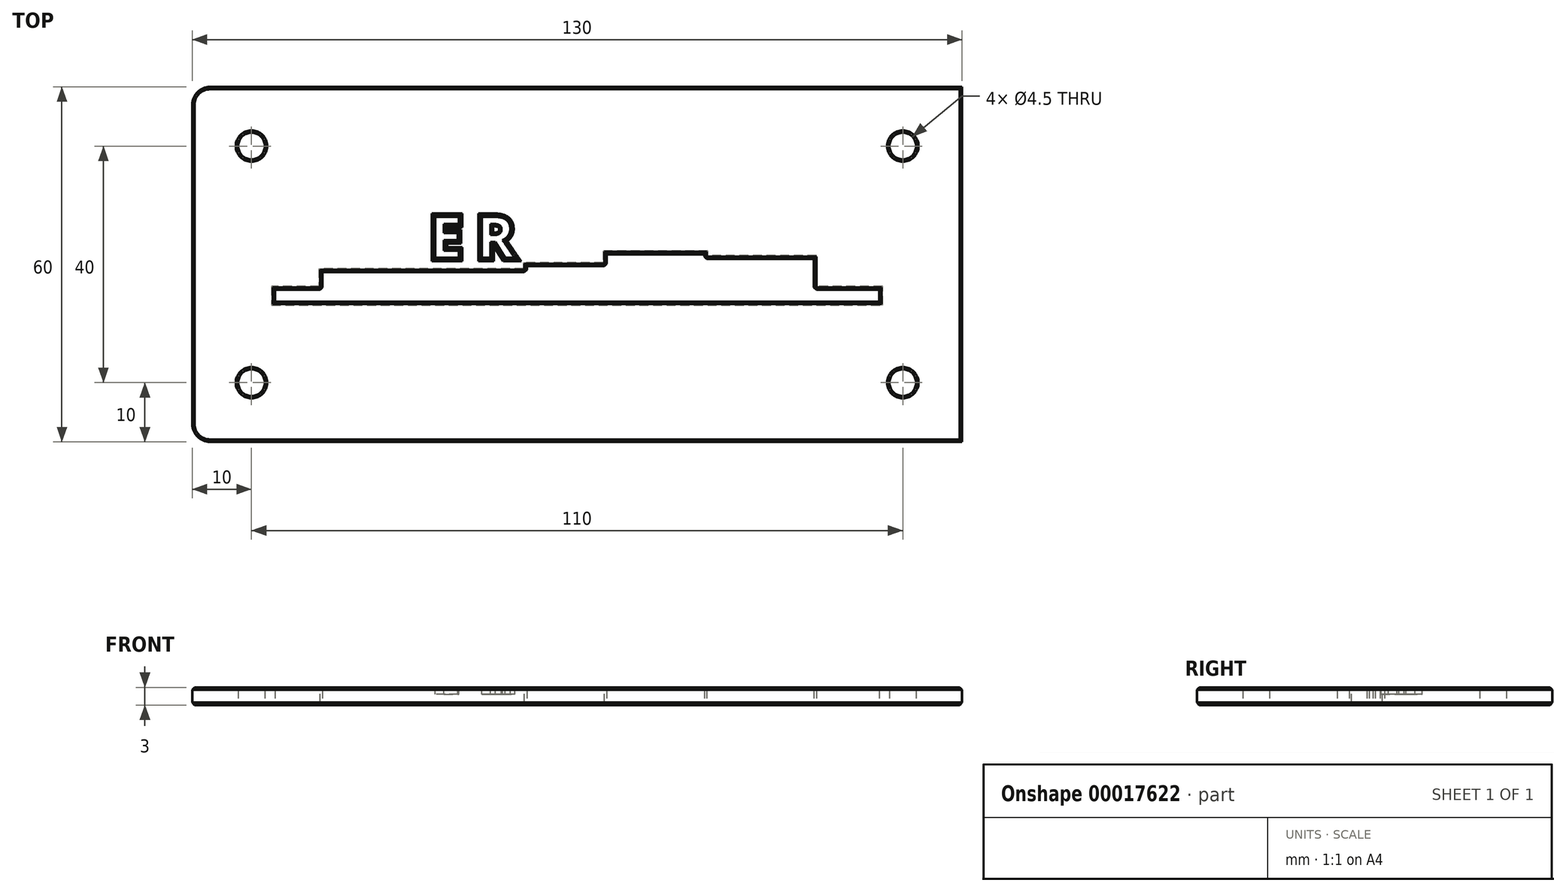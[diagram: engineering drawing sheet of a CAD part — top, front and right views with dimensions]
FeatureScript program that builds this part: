
annotation { "Feature Type Name" : "Feature", "Feature Type Description" : "" }
export const myFeature = defineFeature(function(context is Context, id is Id, definition is map)
    precondition{}
    {
        {
            var Q0;
            Q0=qCreatedBy(makeId("Top.planeOp"),FACE);
            var sketch = newSketch(context, id + "F0", { "sketchPlane" : qUnion([Q0])});
            skLineSegment(sketch, "E0.rect.top", {"start": v(-60, 30) * mm, "end": v(65, 30) * mm});
            skLineSegment(sketch, "E0.rect.right", {"start": v(65, -30) * mm, "end": v(65, 30) * mm});
            skPoint(sketch, "E0.rect.middle", {"position": v(0, 0) * mm});
            skLineSegment(sketch, "E1.bottom", {"start": v(-65, 30) * mm, "end": v(-60, 30) * mm});
            skLineSegment(sketch, "E2.bottom", {"start": v(65, 30) * mm, "end": v(55, 30) * mm});
            skLineSegment(sketch, "E2.left", {"start": v(65, 30) * mm, "end": v(65, 22.5) * mm});
            skLineSegment(sketch, "E3.left", {"start": v(65, -30) * mm, "end": v(65, -22.5) * mm});
            skCircle(sketch, "E4", {"center": v(-55, -20) * mm, "radius": 2.25 * mm});
            skCircle(sketch, "E5", {"center": v(-55, 20) * mm, "radius": 2.25 * mm});
            skCircle(sketch, "E6", {"center": v(55, 20) * mm, "radius": 2.25 * mm});
            skCircle(sketch, "E7", {"center": v(55, -20) * mm, "radius": 2.25 * mm});
            skLineSegment(sketch, "E8", {"start": v(-51, 6.3) * mm, "end": v(1.5, 6.3) * mm});
            skLineSegment(sketch, "E9.top", {"start": v(-51, 4.3) * mm, "end": v(-43, 4.3) * mm});
            skLineSegment(sketch, "E9.left", {"start": v(-51, 6.3) * mm, "end": v(-51, 4.3) * mm});
            skLineSegment(sketch, "E9.right", {"start": v(51, 6.3) * mm, "end": v(51, 4.3) * mm});
            skLineSegment(sketch, "E10.top", {"start": v(-43, 1.3) * mm, "end": v(-8.5, 1.3) * mm});
            skLineSegment(sketch, "E10.left", {"start": v(-43, 4.3) * mm, "end": v(-43, 1.3) * mm});
            skLineSegment(sketch, "E11.trimOffspring", {"start": v(43, 4.3) * mm, "end": v(51, 4.3) * mm});
            skLineSegment(sketch, "E12.right", {"start": v(-8.5, 1.3) * mm, "end": v(-8.5, 0.3) * mm});
            skLineSegment(sketch, "E13.left", {"start": v(-8.5, 0.3) * mm, "end": v(-8.5, 1.3) * mm});
            skLineSegment(sketch, "E14.top", {"start": v(-8.5, 0.3) * mm, "end": v(1.5, 0.3) * mm});
            skLineSegment(sketch, "E15.right", {"start": v(21.5, 1.3) * mm, "end": v(21.5, 1.6) * mm});
            skLineSegment(sketch, "E16.top", {"start": v(5, -1.7) * mm, "end": v(21.5, -1.7) * mm});
            skLineSegment(sketch, "E16.right", {"start": v(21.5, -0.9) * mm, "end": v(21.5, -1.7) * mm});
            skLineSegment(sketch, "E17.trimOffspring", {"start": v(5, 6.3) * mm, "end": v(21.5, 6.3) * mm});
            skLineSegment(sketch, "E18.trimOffspring", {"start": v(25, 6.3) * mm, "end": v(51, 6.3) * mm});
            skLineSegment(sketch, "E19", {"start": v(-43, 4.3) * mm, "end": v(5, 4.3) * mm, "construction": true});
            skLineSegment(sketch, "E20", {"start": v(1.5, 6.3) * mm, "end": v(5, 6.3) * mm});
            skLineSegment(sketch, "E21", {"start": v(21.5, 6.3) * mm, "end": v(25, 6.3) * mm});
            skLineSegment(sketch, "E22.bottom", {"start": v(43, 4.3) * mm, "end": v(40, 4.3) * mm});
            skLineSegment(sketch, "E22.right", {"start": v(40, 4.3) * mm, "end": v(40, 1.6) * mm});
            skPoint(sketch, "E23.oppositeSnap0", {"position": v(25, 1.6) * mm});
            skPoint(sketch, "E24.orphan", {"position": v(43, -10) * mm});
            skLineSegment(sketch, "E25.trimOffspring", {"start": v(40, 4.3) * mm, "end": v(43, 4.3) * mm, "construction": true});
            skPoint(sketch, "E26.orphan", {"position": v(25, -10.7) * mm});
            skPoint(sketch, "E27.right.start.orphan", {"position": v(25, 13.9) * mm});
            skPoint(sketch, "E28.end.orphan", {"position": v(23, 3.6) * mm});
            skLineSegment(sketch, "E29.top", {"start": v(4.98, 0.3) * mm, "end": v(1.5, 0.3) * mm});
            skLineSegment(sketch, "E30", {"start": v(4.98, 0.3) * mm, "end": v(5, -1.7) * mm});
            skLineSegment(sketch, "E31.top", {"start": v(21.5, -0.9) * mm, "end": v(40, -0.9) * mm});
            skLineSegment(sketch, "E31.right", {"start": v(40, 1.6) * mm, "end": v(40, -0.9) * mm});
            skPoint(sketch, "E32.start.orphan", {"position": v(23, 1.6) * mm});
            skLineSegment(sketch, "E33", {"start": v(-65, 30) * mm, "end": v(-65, -30) * mm});
            skPoint(sketch, "E34.orphan", {"position": v(-65, -30) * mm});
            skPoint(sketch, "E0.rect.bottom.start.orphan", {"position": v(60, -30) * mm});
            skLineSegment(sketch, "E35", {"start": v(-65, -30) * mm, "end": v(65, -30) * mm});
            skSolve(sketch);
        }
        {
            var Q0;
            Q0=makeQuery(id+"F0.imprint","IMPRINT",FACE,{"disambiguationData":[TD([[makeQuery(id+"F0.imprint","IMPRINT",EDGE,{"derivedFrom":sQuery(id+"F0.wireOp",EDGE,"E0.rect.bottom")}),1.0]])]});
            var Q1;
            Q1=makeQuery(id+"F0.imprint","IMPRINT",FACE,{"disambiguationData":[TD([[makeQuery(id+"F0.imprint","IMPRINT",EDGE,{"derivedFrom":sQuery(id+"F0.wireOp",EDGE,"E0.rect.top")}),-1.0]])]});
            extrude(context, id + "F1", {"entities" : qUnion([Q0, Q1]), "oppositeDirection" : true, "depth" : 3 * mm, "offsetDistance" : 25 * mm});
        }
        {
            var Q0;
            Q0=makeQuery(id+"F1.opExtrude","SWEPT_EDGE",EDGE,{"disambiguationData":[OSD([sQuery(id+"F0.wireOp",EDGE,"E3.bottom"),sQuery(id+"F0.wireOp",EDGE,"E3.left")])]});
            var Q1;
            Q1=makeQuery(id+"F1.opExtrude","SWEPT_EDGE",EDGE,{"disambiguationData":[OSD([sQuery(id+"F0.wireOp",EDGE,"fb71736d-f74a-4242-934e-06f3cf912558.bottom"),sQuery(id+"F0.wireOp",EDGE,"fb71736d-f74a-4242-934e-06f3cf912558.left")])]});
            var Q2;
            Q2=makeQuery(id+"F1.opExtrude","SWEPT_EDGE",EDGE,{"disambiguationData":[OSD([sQuery(id+"F0.wireOp",EDGE,"E2.bottom"),sQuery(id+"F0.wireOp",EDGE,"E2.left")])]});
            var Q3;
            Q3=makeQuery(id+"F1.opExtrude","SWEPT_EDGE",EDGE,{"disambiguationData":[OSD([sQuery(id+"F0.wireOp",EDGE,"E1.bottom"),sQuery(id+"F0.wireOp",EDGE,"E1.left")])]});
            var Q4;
            Q4=makeQuery(id+"F1.opExtrude","SWEPT_EDGE",EDGE,{"disambiguationData":[OSD([sQuery(id+"F0.wireOp",EDGE,"E33"),sQuery(id+"F0.wireOp",EDGE,"E35")])]});
            fillet(context, id + "F2", {"entities" : qUnion([Q0, Q1, Q2, Q3, Q4]), "radius" : 3 * mm, "tangentPropagation" : true, "allowEdgeOverflow" : false});
        }
        {
            var Q0;
            Q0=makeQuery(id+"F1.opExtrude","CAP_FACE",FACE,{"disambiguationData":[OSD([sQuery(id+"F0.wireOp",EDGE,"E0.rect.bottom"),sQuery(id+"F0.wireOp",EDGE,"E0.rect.top"),sQuery(id+"F0.wireOp",EDGE,"E0.rect.left"),sQuery(id+"F0.wireOp",EDGE,"E0.rect.right"),sQuery(id+"F0.wireOp",EDGE,"fb71736d-f74a-4242-934e-06f3cf912558.bottom"),sQuery(id+"F0.wireOp",EDGE,"fb71736d-f74a-4242-934e-06f3cf912558.left"),sQuery(id+"F0.wireOp",EDGE,"E1.bottom"),sQuery(id+"F0.wireOp",EDGE,"E1.left"),sQuery(id+"F0.wireOp",EDGE,"E2.bottom"),sQuery(id+"F0.wireOp",EDGE,"E2.left"),sQuery(id+"F0.wireOp",EDGE,"E3.bottom"),sQuery(id+"F0.wireOp",EDGE,"E3.left"),sQuery(id+"F0.wireOp",EDGE,"E4"),sQuery(id+"F0.wireOp",EDGE,"E5"),sQuery(id+"F0.wireOp",EDGE,"E6"),sQuery(id+"F0.wireOp",EDGE,"E7"),sQuery(id+"F0.wireOp",EDGE,"E8"),sQuery(id+"F0.wireOp",EDGE,"E9.top"),sQuery(id+"F0.wireOp",EDGE,"E9.left"),sQuery(id+"F0.wireOp",EDGE,"E9.right"),sQuery(id+"F0.wireOp",EDGE,"E10.left"),sQuery(id+"F0.wireOp",EDGE,"E10.right"),sQuery(id+"F0.wireOp",EDGE,"E11.trimOffspring"),sQuery(id+"F0.wireOp",EDGE,"E10.top"),sQuery(id+"F0.wireOp",EDGE,"E13.bottom"),sQuery(id+"F0.wireOp",EDGE,"E13.left"),sQuery(id+"F0.wireOp",EDGE,"E13.right"),sQuery(id+"F0.wireOp",EDGE,"2bbd994b-3e8e-4b0d-a158-f2154df3f7ed.trimOffspring"),sQuery(id+"F0.wireOp",EDGE,"E27.top"),sQuery(id+"F0.wireOp",EDGE,"E27.left"),sQuery(id+"F0.wireOp",EDGE,"E27.right")])],"isStart":false});
            var sketch = newSketch(context, id + "F3", { "sketchPlane" : qUnion([Q0])});
            skText(sketch, "E36", { "text": "E", "fontName": "OpenSans-Bold.ttf"});
            skText(sketch, "E37", { "text": "R", "fontName": "OpenSans-Bold.ttf"});
            skPoint(sketch, "E38.right.start.orphan", {"position": v(-26.9, 1.1) * mm});
            skPoint(sketch, "E39.orphan", {"position": v(-8.9, -0.9) * mm});
            skPoint(sketch, "E38.bottom.end.orphan", {"position": v(-26.9, -0.9) * mm});
            skPoint(sketch, "E38.bottom.start.orphan", {"position": v(-17.9, -0.9) * mm});
            skLineSegment(sketch, "E40", {"start": v(-43, -1.3) * mm, "end": v(-8.5, -1.3) * mm});
            const initialGuessF3  = {"E36": [-0.02483, 0.0011, 1, 0, 0.007], "E37": [-0.01696, 0.0011, 1, 0, 0.007]};
            skSetInitialGuess(sketch, initialGuessF3);
            skSolve(sketch);
        }
        {
            var Q0;
            Q0=makeQuery(id+"F3.imprint","IMPRINT",FACE,{"disambiguationData":[TD([[makeQuery(id+"F3.imprint","IMPRINT",EDGE,{"derivedFrom":sQuery(id+"F3.wireOp",EDGE,"E36.sketch_text.stroke-0")}),-1.0]])]});
            var Q1;
            Q1=makeQuery(id+"F3.imprint","IMPRINT",FACE,{"disambiguationData":[TD([[makeQuery(id+"F3.imprint","IMPRINT",EDGE,{"derivedFrom":sQuery(id+"F3.wireOp",EDGE,"E37.sketch_text.stroke-0")}),-1.0]])]});
            extrude(context, id + "F4", {"entities" : qUnion([Q0, Q1]), "operationType" : NewBodyOperationType.REMOVE, "oppositeDirection" : true, "depth" : 1.2 * mm});
        }
        {
            var Q0;
            Q0=makeQuery(id+"F4.boolean.opBoolean","COPY",EDGE,{"derivedFrom":makeQuery(id+"F4.opExtrude","CAP_EDGE",EDGE,{"disambiguationData":[OSD([sQuery(id+"F3.wireOp",EDGE,"E36.sketch_text.stroke-1")])],"isStart":true})});
            var Q1;
            Q1=makeQuery(id+"F4.boolean.opBoolean","COPY",EDGE,{"derivedFrom":makeQuery(id+"F4.opExtrude","CAP_EDGE",EDGE,{"disambiguationData":[OSD([sQuery(id+"F3.wireOp",EDGE,"E36.sketch_text.stroke-2")])],"isStart":true})});
            var Q2;
            Q2=makeQuery(id+"F4.boolean.opBoolean","COPY",EDGE,{"derivedFrom":makeQuery(id+"F4.opExtrude","CAP_EDGE",EDGE,{"disambiguationData":[OSD([sQuery(id+"F3.wireOp",EDGE,"E36.sketch_text.stroke-3")])],"isStart":true})});
            var Q3;
            Q3=makeQuery(id+"F4.boolean.opBoolean","COPY",EDGE,{"derivedFrom":makeQuery(id+"F4.opExtrude","CAP_EDGE",EDGE,{"disambiguationData":[OSD([sQuery(id+"F3.wireOp",EDGE,"E36.sketch_text.stroke-4")])],"isStart":true})});
            var Q4;
            Q4=makeQuery(id+"F4.boolean.opBoolean","COPY",EDGE,{"derivedFrom":makeQuery(id+"F4.opExtrude","CAP_EDGE",EDGE,{"disambiguationData":[OSD([sQuery(id+"F3.wireOp",EDGE,"E36.sketch_text.stroke-5")])],"isStart":true})});
            var Q5;
            Q5=makeQuery(id+"F4.boolean.opBoolean","COPY",EDGE,{"derivedFrom":makeQuery(id+"F4.opExtrude","CAP_EDGE",EDGE,{"disambiguationData":[OSD([sQuery(id+"F3.wireOp",EDGE,"E36.sketch_text.stroke-6")])],"isStart":true})});
            var Q6;
            Q6=makeQuery(id+"F4.boolean.opBoolean","COPY",EDGE,{"derivedFrom":makeQuery(id+"F4.opExtrude","CAP_EDGE",EDGE,{"disambiguationData":[OSD([sQuery(id+"F3.wireOp",EDGE,"E36.sketch_text.stroke-7")])],"isStart":true})});
            var Q7;
            Q7=makeQuery(id+"F4.boolean.opBoolean","COPY",EDGE,{"derivedFrom":makeQuery(id+"F4.opExtrude","CAP_EDGE",EDGE,{"disambiguationData":[OSD([sQuery(id+"F3.wireOp",EDGE,"E36.sketch_text.stroke-8")])],"isStart":true})});
            var Q8;
            Q8=makeQuery(id+"F4.boolean.opBoolean","COPY",EDGE,{"derivedFrom":makeQuery(id+"F4.opExtrude","CAP_EDGE",EDGE,{"disambiguationData":[OSD([sQuery(id+"F3.wireOp",EDGE,"E36.sketch_text.stroke-9")])],"isStart":true})});
            var Q9;
            Q9=makeQuery(id+"F4.boolean.opBoolean","COPY",EDGE,{"derivedFrom":makeQuery(id+"F4.opExtrude","CAP_EDGE",EDGE,{"disambiguationData":[OSD([sQuery(id+"F3.wireOp",EDGE,"E36.sketch_text.stroke-10")])],"isStart":true})});
            var Q10;
            Q10=makeQuery(id+"F4.boolean.opBoolean","COPY",EDGE,{"derivedFrom":makeQuery(id+"F4.opExtrude","CAP_EDGE",EDGE,{"disambiguationData":[OSD([sQuery(id+"F3.wireOp",EDGE,"E36.sketch_text.stroke-11")])],"isStart":true})});
            var Q11;
            Q11=makeQuery(id+"F4.boolean.opBoolean","COPY",EDGE,{"derivedFrom":makeQuery(id+"F4.opExtrude","CAP_EDGE",EDGE,{"disambiguationData":[OSD([sQuery(id+"F3.wireOp",EDGE,"E36.sketch_text.stroke-0")])],"isStart":true})});
            var Q12;
            Q12=makeQuery(id+"F4.boolean.opBoolean","COPY",EDGE,{"derivedFrom":makeQuery(id+"F4.opExtrude","CAP_EDGE",EDGE,{"disambiguationData":[OSD([sQuery(id+"F3.wireOp",EDGE,"E37.sketch_text.stroke-9")])],"isStart":true})});
            var Q13;
            Q13=makeQuery(id+"F4.boolean.opBoolean","COPY",EDGE,{"derivedFrom":makeQuery(id+"F4.opExtrude","CAP_EDGE",EDGE,{"disambiguationData":[OSD([sQuery(id+"F3.wireOp",EDGE,"E37.sketch_text.stroke-8")])],"isStart":true})});
            var Q14;
            Q14=makeQuery(id+"F4.boolean.opBoolean","COPY",EDGE,{"derivedFrom":makeQuery(id+"F4.opExtrude","CAP_EDGE",EDGE,{"disambiguationData":[OSD([sQuery(id+"F3.wireOp",EDGE,"E37.sketch_text.stroke-7")])],"isStart":true})});
            var Q15;
            Q15=makeQuery(id+"F4.boolean.opBoolean","COPY",EDGE,{"derivedFrom":makeQuery(id+"F4.opExtrude","CAP_EDGE",EDGE,{"disambiguationData":[OSD([sQuery(id+"F3.wireOp",EDGE,"E37.sketch_text.stroke-18")])],"isStart":true})});
            var Q16;
            Q16=makeQuery(id+"F4.boolean.opBoolean","COPY",EDGE,{"derivedFrom":makeQuery(id+"F4.opExtrude","CAP_EDGE",EDGE,{"disambiguationData":[OSD([sQuery(id+"F3.wireOp",EDGE,"E37.sketch_text.stroke-17")])],"isStart":true})});
            var Q17;
            Q17=makeQuery(id+"F4.boolean.opBoolean","COPY",EDGE,{"derivedFrom":makeQuery(id+"F4.opExtrude","CAP_EDGE",EDGE,{"disambiguationData":[OSD([sQuery(id+"F3.wireOp",EDGE,"E37.sketch_text.stroke-16")])],"isStart":true})});
            var Q18;
            Q18=makeQuery(id+"F4.boolean.opBoolean","COPY",EDGE,{"derivedFrom":makeQuery(id+"F4.opExtrude","CAP_EDGE",EDGE,{"disambiguationData":[OSD([sQuery(id+"F3.wireOp",EDGE,"E37.sketch_text.stroke-15")])],"isStart":true})});
            var Q19;
            Q19=makeQuery(id+"F4.boolean.opBoolean","COPY",EDGE,{"derivedFrom":makeQuery(id+"F4.opExtrude","CAP_EDGE",EDGE,{"disambiguationData":[OSD([sQuery(id+"F3.wireOp",EDGE,"E37.sketch_text.stroke-14")])],"isStart":true})});
            var Q20;
            Q20=makeQuery(id+"F4.boolean.opBoolean","COPY",EDGE,{"derivedFrom":makeQuery(id+"F4.opExtrude","CAP_EDGE",EDGE,{"disambiguationData":[OSD([sQuery(id+"F3.wireOp",EDGE,"E37.sketch_text.stroke-13")])],"isStart":true})});
            var Q21;
            Q21=makeQuery(id+"F4.boolean.opBoolean","COPY",EDGE,{"derivedFrom":makeQuery(id+"F4.opExtrude","CAP_EDGE",EDGE,{"disambiguationData":[OSD([sQuery(id+"F3.wireOp",EDGE,"E37.sketch_text.stroke-12")])],"isStart":true})});
            var Q22;
            Q22=makeQuery(id+"F4.boolean.opBoolean","COPY",EDGE,{"derivedFrom":makeQuery(id+"F4.opExtrude","CAP_EDGE",EDGE,{"disambiguationData":[OSD([sQuery(id+"F3.wireOp",EDGE,"E37.sketch_text.stroke-11")])],"isStart":true})});
            var Q23;
            Q23=makeQuery(id+"F4.boolean.opBoolean","COPY",EDGE,{"derivedFrom":makeQuery(id+"F4.opExtrude","CAP_EDGE",EDGE,{"disambiguationData":[OSD([sQuery(id+"F3.wireOp",EDGE,"E37.sketch_text.stroke-10")])],"isStart":true})});
            var Q24;
            Q24=makeQuery(id+"F4.boolean.opBoolean","SPLIT",FACE,{"disambiguationData":[TD([makeQuery(id+"F4.opExtrude","SWEPT_FACE",FACE,{"disambiguationData":[OSD([sQuery(id+"F3.wireOp",EDGE,"E37.sketch_text.stroke-0")])]})])],"derivedFrom":makeQuery(id+"F1.opExtrude","CAP_FACE",FACE,{"disambiguationData":[OSD([sQuery(id+"F0.wireOp",EDGE,"E0.rect.bottom"),sQuery(id+"F0.wireOp",EDGE,"E0.rect.top"),sQuery(id+"F0.wireOp",EDGE,"E0.rect.left"),sQuery(id+"F0.wireOp",EDGE,"E0.rect.right"),sQuery(id+"F0.wireOp",EDGE,"fb71736d-f74a-4242-934e-06f3cf912558.left"),sQuery(id+"F0.wireOp",EDGE,"E1.bottom"),sQuery(id+"F0.wireOp",EDGE,"E1.left"),sQuery(id+"F0.wireOp",EDGE,"E2.bottom"),sQuery(id+"F0.wireOp",EDGE,"E2.left"),sQuery(id+"F0.wireOp",EDGE,"E3.bottom"),sQuery(id+"F0.wireOp",EDGE,"E3.left"),sQuery(id+"F0.wireOp",EDGE,"E4"),sQuery(id+"F0.wireOp",EDGE,"E5"),sQuery(id+"F0.wireOp",EDGE,"E6"),sQuery(id+"F0.wireOp",EDGE,"E7"),sQuery(id+"F0.wireOp",EDGE,"E8"),sQuery(id+"F0.wireOp",EDGE,"E9.top"),sQuery(id+"F0.wireOp",EDGE,"E9.left"),sQuery(id+"F0.wireOp",EDGE,"E9.right"),sQuery(id+"F0.wireOp",EDGE,"E10.left"),sQuery(id+"F0.wireOp",EDGE,"E10.right"),sQuery(id+"F0.wireOp",EDGE,"E11.trimOffspring"),sQuery(id+"F0.wireOp",EDGE,"E10.top"),sQuery(id+"F0.wireOp",EDGE,"E27.top"),sQuery(id+"F0.wireOp",EDGE,"E27.left"),sQuery(id+"F0.wireOp",EDGE,"E27.right"),sQuery(id+"F0.wireOp",EDGE,"E14.top"),sQuery(id+"F0.wireOp",EDGE,"E12.right"),sQuery(id+"F0.wireOp",EDGE,"E14.right"),sQuery(id+"F0.wireOp",EDGE,"c10e0dd7-fc39-4358-877f-853744283f95"),sQuery(id+"F0.wireOp",EDGE,"E15.left"),sQuery(id+"F0.wireOp",EDGE,"E15.right"),sQuery(id+"F0.wireOp",EDGE,"b61ca566-ba07-4bff-9836-ffdb72489c4c.left"),sQuery(id+"F0.wireOp",EDGE,"b61ca566-ba07-4bff-9836-ffdb72489c4c.right"),sQuery(id+"F0.wireOp",EDGE,"E16.top"),sQuery(id+"F0.wireOp",EDGE,"E16.left"),sQuery(id+"F0.wireOp",EDGE,"E16.right"),sQuery(id+"F0.wireOp",EDGE,"E17.trimOffspring"),sQuery(id+"F0.wireOp",EDGE,"E18.trimOffspring"),sQuery(id+"F0.wireOp",EDGE,"54661143-fa5e-42c1-9d10-70f3552f3fbd"),sQuery(id+"F0.wireOp",EDGE,"E28"),sQuery(id+"F0.wireOp",EDGE,"E20"),sQuery(id+"F0.wireOp",EDGE,"E21")])],"isStart":false})});
            chamfer(context, id + "F5", {"entities" : qUnion([Q0, Q1, Q2, Q3, Q4, Q5, Q6, Q7, Q8, Q9, Q10, Q11, Q12, Q13, Q14, Q15, Q16, Q17, Q18, Q19, Q20, Q21, Q22, Q23, Q24]), "width" : .4 * mm});
        }
        {
            var Q0;
            Q0=makeQuery(id+"F1.opExtrude","CAP_EDGE",EDGE,{"disambiguationData":[OSD([sQuery(id+"F0.wireOp",EDGE,"E0.rect.bottom"),sQuery(id+"F0.wireOp",EDGE,"E3.bottom"),sQuery(id+"F0.wireOp",EDGE,"c10e0dd7-fc39-4358-877f-853744283f95")])],"isStart":false});
            var Q1;
            {var subQ0=sQuery(id+"F0.wireOp",EDGE,"fb71736d-f74a-4242-934e-06f3cf912558.left");var subQ1=sQuery(id+"F0.wireOp",EDGE,"c10e0dd7-fc39-4358-877f-853744283f95");Q1=makeQuery(id+"F2.opFillet","BLEND_EDGE",EDGE,{"blendedFrom":[makeQuery(id+"F1.opExtrude","SWEPT_EDGE",EDGE,{"disambiguationData":[OSD([subQ0,subQ1])]}),makeQuery(id+"F1.opExtrude","CAP_FACE",FACE,{"disambiguationData":[OSD([sQuery(id+"F0.wireOp",EDGE,"E0.rect.bottom"),sQuery(id+"F0.wireOp",EDGE,"E0.rect.top"),sQuery(id+"F0.wireOp",EDGE,"E0.rect.left"),sQuery(id+"F0.wireOp",EDGE,"E0.rect.right"),subQ0,sQuery(id+"F0.wireOp",EDGE,"E1.bottom"),sQuery(id+"F0.wireOp",EDGE,"E1.left"),sQuery(id+"F0.wireOp",EDGE,"E2.bottom"),sQuery(id+"F0.wireOp",EDGE,"E2.left"),sQuery(id+"F0.wireOp",EDGE,"E3.bottom"),sQuery(id+"F0.wireOp",EDGE,"E3.left"),sQuery(id+"F0.wireOp",EDGE,"E4"),sQuery(id+"F0.wireOp",EDGE,"E5"),sQuery(id+"F0.wireOp",EDGE,"E6"),sQuery(id+"F0.wireOp",EDGE,"E7"),sQuery(id+"F0.wireOp",EDGE,"E8"),sQuery(id+"F0.wireOp",EDGE,"E9.top"),sQuery(id+"F0.wireOp",EDGE,"E9.left"),sQuery(id+"F0.wireOp",EDGE,"E9.right"),sQuery(id+"F0.wireOp",EDGE,"E10.left"),sQuery(id+"F0.wireOp",EDGE,"E10.right"),sQuery(id+"F0.wireOp",EDGE,"E11.trimOffspring"),sQuery(id+"F0.wireOp",EDGE,"E10.top"),sQuery(id+"F0.wireOp",EDGE,"E27.top"),sQuery(id+"F0.wireOp",EDGE,"E27.left"),sQuery(id+"F0.wireOp",EDGE,"E27.right"),sQuery(id+"F0.wireOp",EDGE,"E14.top"),sQuery(id+"F0.wireOp",EDGE,"E12.right"),sQuery(id+"F0.wireOp",EDGE,"E14.right"),subQ1,sQuery(id+"F0.wireOp",EDGE,"E15.left"),sQuery(id+"F0.wireOp",EDGE,"E15.right"),sQuery(id+"F0.wireOp",EDGE,"b61ca566-ba07-4bff-9836-ffdb72489c4c.left"),sQuery(id+"F0.wireOp",EDGE,"b61ca566-ba07-4bff-9836-ffdb72489c4c.right"),sQuery(id+"F0.wireOp",EDGE,"E16.top"),sQuery(id+"F0.wireOp",EDGE,"E16.left"),sQuery(id+"F0.wireOp",EDGE,"E16.right"),sQuery(id+"F0.wireOp",EDGE,"E17.trimOffspring"),sQuery(id+"F0.wireOp",EDGE,"E18.trimOffspring"),sQuery(id+"F0.wireOp",EDGE,"54661143-fa5e-42c1-9d10-70f3552f3fbd"),sQuery(id+"F0.wireOp",EDGE,"E28"),sQuery(id+"F0.wireOp",EDGE,"E20"),sQuery(id+"F0.wireOp",EDGE,"E21")])],"isStart":false})],"blendedInto":[makeQuery(id+"F1.opExtrude","CAP_FACE",FACE,{"disambiguationData":[OSD([sQuery(id+"F0.wireOp",EDGE,"E0.rect.bottom"),sQuery(id+"F0.wireOp",EDGE,"E0.rect.top"),sQuery(id+"F0.wireOp",EDGE,"E0.rect.left"),sQuery(id+"F0.wireOp",EDGE,"E0.rect.right"),subQ0,sQuery(id+"F0.wireOp",EDGE,"E1.bottom"),sQuery(id+"F0.wireOp",EDGE,"E1.left"),sQuery(id+"F0.wireOp",EDGE,"E2.bottom"),sQuery(id+"F0.wireOp",EDGE,"E2.left"),sQuery(id+"F0.wireOp",EDGE,"E3.bottom"),sQuery(id+"F0.wireOp",EDGE,"E3.left"),sQuery(id+"F0.wireOp",EDGE,"E4"),sQuery(id+"F0.wireOp",EDGE,"E5"),sQuery(id+"F0.wireOp",EDGE,"E6"),sQuery(id+"F0.wireOp",EDGE,"E7"),sQuery(id+"F0.wireOp",EDGE,"E8"),sQuery(id+"F0.wireOp",EDGE,"E9.top"),sQuery(id+"F0.wireOp",EDGE,"E9.left"),sQuery(id+"F0.wireOp",EDGE,"E9.right"),sQuery(id+"F0.wireOp",EDGE,"E10.left"),sQuery(id+"F0.wireOp",EDGE,"E10.right"),sQuery(id+"F0.wireOp",EDGE,"E11.trimOffspring"),sQuery(id+"F0.wireOp",EDGE,"E10.top"),sQuery(id+"F0.wireOp",EDGE,"E27.top"),sQuery(id+"F0.wireOp",EDGE,"E27.left"),sQuery(id+"F0.wireOp",EDGE,"E27.right"),sQuery(id+"F0.wireOp",EDGE,"E14.top"),sQuery(id+"F0.wireOp",EDGE,"E12.right"),sQuery(id+"F0.wireOp",EDGE,"E14.right"),subQ1,sQuery(id+"F0.wireOp",EDGE,"E15.left"),sQuery(id+"F0.wireOp",EDGE,"E15.right"),sQuery(id+"F0.wireOp",EDGE,"b61ca566-ba07-4bff-9836-ffdb72489c4c.left"),sQuery(id+"F0.wireOp",EDGE,"b61ca566-ba07-4bff-9836-ffdb72489c4c.right"),sQuery(id+"F0.wireOp",EDGE,"E16.top"),sQuery(id+"F0.wireOp",EDGE,"E16.left"),sQuery(id+"F0.wireOp",EDGE,"E16.right"),sQuery(id+"F0.wireOp",EDGE,"E17.trimOffspring"),sQuery(id+"F0.wireOp",EDGE,"E18.trimOffspring"),sQuery(id+"F0.wireOp",EDGE,"54661143-fa5e-42c1-9d10-70f3552f3fbd"),sQuery(id+"F0.wireOp",EDGE,"E28"),sQuery(id+"F0.wireOp",EDGE,"E20"),sQuery(id+"F0.wireOp",EDGE,"E21")])],"isStart":false})]});}
            var Q2;
            Q2=makeQuery(id+"F1.opExtrude","CAP_EDGE",EDGE,{"disambiguationData":[OSD([sQuery(id+"F0.wireOp",EDGE,"E0.rect.left"),sQuery(id+"F0.wireOp",EDGE,"fb71736d-f74a-4242-934e-06f3cf912558.left"),sQuery(id+"F0.wireOp",EDGE,"E1.left")])],"isStart":false});
            var Q3;
            {var subQ0=sQuery(id+"F0.wireOp",EDGE,"E3.bottom");var subQ1=sQuery(id+"F0.wireOp",EDGE,"E3.left");Q3=makeQuery(id+"F2.opFillet","BLEND_EDGE",EDGE,{"blendedFrom":[makeQuery(id+"F1.opExtrude","SWEPT_EDGE",EDGE,{"disambiguationData":[OSD([subQ0,subQ1])]}),makeQuery(id+"F1.opExtrude","CAP_FACE",FACE,{"disambiguationData":[OSD([sQuery(id+"F0.wireOp",EDGE,"E0.rect.bottom"),sQuery(id+"F0.wireOp",EDGE,"E0.rect.top"),sQuery(id+"F0.wireOp",EDGE,"E0.rect.left"),sQuery(id+"F0.wireOp",EDGE,"E0.rect.right"),sQuery(id+"F0.wireOp",EDGE,"fb71736d-f74a-4242-934e-06f3cf912558.left"),sQuery(id+"F0.wireOp",EDGE,"E1.bottom"),sQuery(id+"F0.wireOp",EDGE,"E1.left"),sQuery(id+"F0.wireOp",EDGE,"E2.bottom"),sQuery(id+"F0.wireOp",EDGE,"E2.left"),subQ0,subQ1,sQuery(id+"F0.wireOp",EDGE,"E4"),sQuery(id+"F0.wireOp",EDGE,"E5"),sQuery(id+"F0.wireOp",EDGE,"E6"),sQuery(id+"F0.wireOp",EDGE,"E7"),sQuery(id+"F0.wireOp",EDGE,"E8"),sQuery(id+"F0.wireOp",EDGE,"E9.top"),sQuery(id+"F0.wireOp",EDGE,"E9.left"),sQuery(id+"F0.wireOp",EDGE,"E9.right"),sQuery(id+"F0.wireOp",EDGE,"E10.left"),sQuery(id+"F0.wireOp",EDGE,"E10.right"),sQuery(id+"F0.wireOp",EDGE,"E11.trimOffspring"),sQuery(id+"F0.wireOp",EDGE,"E10.top"),sQuery(id+"F0.wireOp",EDGE,"E27.top"),sQuery(id+"F0.wireOp",EDGE,"E27.left"),sQuery(id+"F0.wireOp",EDGE,"E27.right"),sQuery(id+"F0.wireOp",EDGE,"E14.top"),sQuery(id+"F0.wireOp",EDGE,"E12.right"),sQuery(id+"F0.wireOp",EDGE,"E14.right"),sQuery(id+"F0.wireOp",EDGE,"c10e0dd7-fc39-4358-877f-853744283f95"),sQuery(id+"F0.wireOp",EDGE,"E15.left"),sQuery(id+"F0.wireOp",EDGE,"E15.right"),sQuery(id+"F0.wireOp",EDGE,"b61ca566-ba07-4bff-9836-ffdb72489c4c.left"),sQuery(id+"F0.wireOp",EDGE,"b61ca566-ba07-4bff-9836-ffdb72489c4c.right"),sQuery(id+"F0.wireOp",EDGE,"E16.top"),sQuery(id+"F0.wireOp",EDGE,"E16.left"),sQuery(id+"F0.wireOp",EDGE,"E16.right"),sQuery(id+"F0.wireOp",EDGE,"E17.trimOffspring"),sQuery(id+"F0.wireOp",EDGE,"E18.trimOffspring"),sQuery(id+"F0.wireOp",EDGE,"54661143-fa5e-42c1-9d10-70f3552f3fbd"),sQuery(id+"F0.wireOp",EDGE,"E28"),sQuery(id+"F0.wireOp",EDGE,"E20"),sQuery(id+"F0.wireOp",EDGE,"E21")])],"isStart":false})],"blendedInto":[makeQuery(id+"F1.opExtrude","CAP_FACE",FACE,{"disambiguationData":[OSD([sQuery(id+"F0.wireOp",EDGE,"E0.rect.bottom"),sQuery(id+"F0.wireOp",EDGE,"E0.rect.top"),sQuery(id+"F0.wireOp",EDGE,"E0.rect.left"),sQuery(id+"F0.wireOp",EDGE,"E0.rect.right"),sQuery(id+"F0.wireOp",EDGE,"fb71736d-f74a-4242-934e-06f3cf912558.left"),sQuery(id+"F0.wireOp",EDGE,"E1.bottom"),sQuery(id+"F0.wireOp",EDGE,"E1.left"),sQuery(id+"F0.wireOp",EDGE,"E2.bottom"),sQuery(id+"F0.wireOp",EDGE,"E2.left"),subQ0,subQ1,sQuery(id+"F0.wireOp",EDGE,"E4"),sQuery(id+"F0.wireOp",EDGE,"E5"),sQuery(id+"F0.wireOp",EDGE,"E6"),sQuery(id+"F0.wireOp",EDGE,"E7"),sQuery(id+"F0.wireOp",EDGE,"E8"),sQuery(id+"F0.wireOp",EDGE,"E9.top"),sQuery(id+"F0.wireOp",EDGE,"E9.left"),sQuery(id+"F0.wireOp",EDGE,"E9.right"),sQuery(id+"F0.wireOp",EDGE,"E10.left"),sQuery(id+"F0.wireOp",EDGE,"E10.right"),sQuery(id+"F0.wireOp",EDGE,"E11.trimOffspring"),sQuery(id+"F0.wireOp",EDGE,"E10.top"),sQuery(id+"F0.wireOp",EDGE,"E27.top"),sQuery(id+"F0.wireOp",EDGE,"E27.left"),sQuery(id+"F0.wireOp",EDGE,"E27.right"),sQuery(id+"F0.wireOp",EDGE,"E14.top"),sQuery(id+"F0.wireOp",EDGE,"E12.right"),sQuery(id+"F0.wireOp",EDGE,"E14.right"),sQuery(id+"F0.wireOp",EDGE,"c10e0dd7-fc39-4358-877f-853744283f95"),sQuery(id+"F0.wireOp",EDGE,"E15.left"),sQuery(id+"F0.wireOp",EDGE,"E15.right"),sQuery(id+"F0.wireOp",EDGE,"b61ca566-ba07-4bff-9836-ffdb72489c4c.left"),sQuery(id+"F0.wireOp",EDGE,"b61ca566-ba07-4bff-9836-ffdb72489c4c.right"),sQuery(id+"F0.wireOp",EDGE,"E16.top"),sQuery(id+"F0.wireOp",EDGE,"E16.left"),sQuery(id+"F0.wireOp",EDGE,"E16.right"),sQuery(id+"F0.wireOp",EDGE,"E17.trimOffspring"),sQuery(id+"F0.wireOp",EDGE,"E18.trimOffspring"),sQuery(id+"F0.wireOp",EDGE,"54661143-fa5e-42c1-9d10-70f3552f3fbd"),sQuery(id+"F0.wireOp",EDGE,"E28"),sQuery(id+"F0.wireOp",EDGE,"E20"),sQuery(id+"F0.wireOp",EDGE,"E21")])],"isStart":false})]});}
            var Q4;
            Q4=makeQuery(id+"F1.opExtrude","CAP_EDGE",EDGE,{"disambiguationData":[OSD([sQuery(id+"F0.wireOp",EDGE,"E0.rect.right"),sQuery(id+"F0.wireOp",EDGE,"E2.left"),sQuery(id+"F0.wireOp",EDGE,"E3.left")])],"isStart":false});
            var Q5;
            {var subQ0=sQuery(id+"F0.wireOp",EDGE,"E2.bottom");var subQ1=sQuery(id+"F0.wireOp",EDGE,"E2.left");Q5=makeQuery(id+"F2.opFillet","BLEND_EDGE",EDGE,{"blendedFrom":[makeQuery(id+"F1.opExtrude","SWEPT_EDGE",EDGE,{"disambiguationData":[OSD([subQ0,subQ1])]}),makeQuery(id+"F1.opExtrude","CAP_FACE",FACE,{"disambiguationData":[OSD([sQuery(id+"F0.wireOp",EDGE,"E0.rect.bottom"),sQuery(id+"F0.wireOp",EDGE,"E0.rect.top"),sQuery(id+"F0.wireOp",EDGE,"E0.rect.left"),sQuery(id+"F0.wireOp",EDGE,"E0.rect.right"),sQuery(id+"F0.wireOp",EDGE,"fb71736d-f74a-4242-934e-06f3cf912558.left"),sQuery(id+"F0.wireOp",EDGE,"E1.bottom"),sQuery(id+"F0.wireOp",EDGE,"E1.left"),subQ0,subQ1,sQuery(id+"F0.wireOp",EDGE,"E3.bottom"),sQuery(id+"F0.wireOp",EDGE,"E3.left"),sQuery(id+"F0.wireOp",EDGE,"E4"),sQuery(id+"F0.wireOp",EDGE,"E5"),sQuery(id+"F0.wireOp",EDGE,"E6"),sQuery(id+"F0.wireOp",EDGE,"E7"),sQuery(id+"F0.wireOp",EDGE,"E8"),sQuery(id+"F0.wireOp",EDGE,"E9.top"),sQuery(id+"F0.wireOp",EDGE,"E9.left"),sQuery(id+"F0.wireOp",EDGE,"E9.right"),sQuery(id+"F0.wireOp",EDGE,"E10.left"),sQuery(id+"F0.wireOp",EDGE,"E10.right"),sQuery(id+"F0.wireOp",EDGE,"E11.trimOffspring"),sQuery(id+"F0.wireOp",EDGE,"E10.top"),sQuery(id+"F0.wireOp",EDGE,"E27.top"),sQuery(id+"F0.wireOp",EDGE,"E27.left"),sQuery(id+"F0.wireOp",EDGE,"E27.right"),sQuery(id+"F0.wireOp",EDGE,"E14.top"),sQuery(id+"F0.wireOp",EDGE,"E12.right"),sQuery(id+"F0.wireOp",EDGE,"E14.right"),sQuery(id+"F0.wireOp",EDGE,"c10e0dd7-fc39-4358-877f-853744283f95"),sQuery(id+"F0.wireOp",EDGE,"E15.left"),sQuery(id+"F0.wireOp",EDGE,"E15.right"),sQuery(id+"F0.wireOp",EDGE,"b61ca566-ba07-4bff-9836-ffdb72489c4c.left"),sQuery(id+"F0.wireOp",EDGE,"b61ca566-ba07-4bff-9836-ffdb72489c4c.right"),sQuery(id+"F0.wireOp",EDGE,"E16.top"),sQuery(id+"F0.wireOp",EDGE,"E16.left"),sQuery(id+"F0.wireOp",EDGE,"E16.right"),sQuery(id+"F0.wireOp",EDGE,"E17.trimOffspring"),sQuery(id+"F0.wireOp",EDGE,"E18.trimOffspring"),sQuery(id+"F0.wireOp",EDGE,"54661143-fa5e-42c1-9d10-70f3552f3fbd"),sQuery(id+"F0.wireOp",EDGE,"E28"),sQuery(id+"F0.wireOp",EDGE,"E20"),sQuery(id+"F0.wireOp",EDGE,"E21")])],"isStart":false})],"blendedInto":[makeQuery(id+"F1.opExtrude","CAP_FACE",FACE,{"disambiguationData":[OSD([sQuery(id+"F0.wireOp",EDGE,"E0.rect.bottom"),sQuery(id+"F0.wireOp",EDGE,"E0.rect.top"),sQuery(id+"F0.wireOp",EDGE,"E0.rect.left"),sQuery(id+"F0.wireOp",EDGE,"E0.rect.right"),sQuery(id+"F0.wireOp",EDGE,"fb71736d-f74a-4242-934e-06f3cf912558.left"),sQuery(id+"F0.wireOp",EDGE,"E1.bottom"),sQuery(id+"F0.wireOp",EDGE,"E1.left"),subQ0,subQ1,sQuery(id+"F0.wireOp",EDGE,"E3.bottom"),sQuery(id+"F0.wireOp",EDGE,"E3.left"),sQuery(id+"F0.wireOp",EDGE,"E4"),sQuery(id+"F0.wireOp",EDGE,"E5"),sQuery(id+"F0.wireOp",EDGE,"E6"),sQuery(id+"F0.wireOp",EDGE,"E7"),sQuery(id+"F0.wireOp",EDGE,"E8"),sQuery(id+"F0.wireOp",EDGE,"E9.top"),sQuery(id+"F0.wireOp",EDGE,"E9.left"),sQuery(id+"F0.wireOp",EDGE,"E9.right"),sQuery(id+"F0.wireOp",EDGE,"E10.left"),sQuery(id+"F0.wireOp",EDGE,"E10.right"),sQuery(id+"F0.wireOp",EDGE,"E11.trimOffspring"),sQuery(id+"F0.wireOp",EDGE,"E10.top"),sQuery(id+"F0.wireOp",EDGE,"E27.top"),sQuery(id+"F0.wireOp",EDGE,"E27.left"),sQuery(id+"F0.wireOp",EDGE,"E27.right"),sQuery(id+"F0.wireOp",EDGE,"E14.top"),sQuery(id+"F0.wireOp",EDGE,"E12.right"),sQuery(id+"F0.wireOp",EDGE,"E14.right"),sQuery(id+"F0.wireOp",EDGE,"c10e0dd7-fc39-4358-877f-853744283f95"),sQuery(id+"F0.wireOp",EDGE,"E15.left"),sQuery(id+"F0.wireOp",EDGE,"E15.right"),sQuery(id+"F0.wireOp",EDGE,"b61ca566-ba07-4bff-9836-ffdb72489c4c.left"),sQuery(id+"F0.wireOp",EDGE,"b61ca566-ba07-4bff-9836-ffdb72489c4c.right"),sQuery(id+"F0.wireOp",EDGE,"E16.top"),sQuery(id+"F0.wireOp",EDGE,"E16.left"),sQuery(id+"F0.wireOp",EDGE,"E16.right"),sQuery(id+"F0.wireOp",EDGE,"E17.trimOffspring"),sQuery(id+"F0.wireOp",EDGE,"E18.trimOffspring"),sQuery(id+"F0.wireOp",EDGE,"54661143-fa5e-42c1-9d10-70f3552f3fbd"),sQuery(id+"F0.wireOp",EDGE,"E28"),sQuery(id+"F0.wireOp",EDGE,"E20"),sQuery(id+"F0.wireOp",EDGE,"E21")])],"isStart":false})]});}
            var Q6;
            Q6=makeQuery(id+"F1.opExtrude","CAP_EDGE",EDGE,{"disambiguationData":[OSD([sQuery(id+"F0.wireOp",EDGE,"E0.rect.top"),sQuery(id+"F0.wireOp",EDGE,"E1.bottom"),sQuery(id+"F0.wireOp",EDGE,"E2.bottom")])],"isStart":false});
            var Q7;
            {var subQ0=sQuery(id+"F0.wireOp",EDGE,"E1.bottom");var subQ1=sQuery(id+"F0.wireOp",EDGE,"E1.left");Q7=makeQuery(id+"F2.opFillet","BLEND_EDGE",EDGE,{"blendedFrom":[makeQuery(id+"F1.opExtrude","SWEPT_EDGE",EDGE,{"disambiguationData":[OSD([subQ0,subQ1])]}),makeQuery(id+"F1.opExtrude","CAP_FACE",FACE,{"disambiguationData":[OSD([sQuery(id+"F0.wireOp",EDGE,"E0.rect.bottom"),sQuery(id+"F0.wireOp",EDGE,"E0.rect.top"),sQuery(id+"F0.wireOp",EDGE,"E0.rect.left"),sQuery(id+"F0.wireOp",EDGE,"E0.rect.right"),sQuery(id+"F0.wireOp",EDGE,"fb71736d-f74a-4242-934e-06f3cf912558.left"),subQ0,subQ1,sQuery(id+"F0.wireOp",EDGE,"E2.bottom"),sQuery(id+"F0.wireOp",EDGE,"E2.left"),sQuery(id+"F0.wireOp",EDGE,"E3.bottom"),sQuery(id+"F0.wireOp",EDGE,"E3.left"),sQuery(id+"F0.wireOp",EDGE,"E4"),sQuery(id+"F0.wireOp",EDGE,"E5"),sQuery(id+"F0.wireOp",EDGE,"E6"),sQuery(id+"F0.wireOp",EDGE,"E7"),sQuery(id+"F0.wireOp",EDGE,"E8"),sQuery(id+"F0.wireOp",EDGE,"E9.top"),sQuery(id+"F0.wireOp",EDGE,"E9.left"),sQuery(id+"F0.wireOp",EDGE,"E9.right"),sQuery(id+"F0.wireOp",EDGE,"E10.left"),sQuery(id+"F0.wireOp",EDGE,"E10.right"),sQuery(id+"F0.wireOp",EDGE,"E11.trimOffspring"),sQuery(id+"F0.wireOp",EDGE,"E10.top"),sQuery(id+"F0.wireOp",EDGE,"E27.top"),sQuery(id+"F0.wireOp",EDGE,"E27.left"),sQuery(id+"F0.wireOp",EDGE,"E27.right"),sQuery(id+"F0.wireOp",EDGE,"E14.top"),sQuery(id+"F0.wireOp",EDGE,"E12.right"),sQuery(id+"F0.wireOp",EDGE,"E14.right"),sQuery(id+"F0.wireOp",EDGE,"c10e0dd7-fc39-4358-877f-853744283f95"),sQuery(id+"F0.wireOp",EDGE,"E15.left"),sQuery(id+"F0.wireOp",EDGE,"E15.right"),sQuery(id+"F0.wireOp",EDGE,"b61ca566-ba07-4bff-9836-ffdb72489c4c.left"),sQuery(id+"F0.wireOp",EDGE,"b61ca566-ba07-4bff-9836-ffdb72489c4c.right"),sQuery(id+"F0.wireOp",EDGE,"E16.top"),sQuery(id+"F0.wireOp",EDGE,"E16.left"),sQuery(id+"F0.wireOp",EDGE,"E16.right"),sQuery(id+"F0.wireOp",EDGE,"E17.trimOffspring"),sQuery(id+"F0.wireOp",EDGE,"E18.trimOffspring"),sQuery(id+"F0.wireOp",EDGE,"54661143-fa5e-42c1-9d10-70f3552f3fbd"),sQuery(id+"F0.wireOp",EDGE,"E28"),sQuery(id+"F0.wireOp",EDGE,"E20"),sQuery(id+"F0.wireOp",EDGE,"E21")])],"isStart":false})],"blendedInto":[makeQuery(id+"F1.opExtrude","CAP_FACE",FACE,{"disambiguationData":[OSD([sQuery(id+"F0.wireOp",EDGE,"E0.rect.bottom"),sQuery(id+"F0.wireOp",EDGE,"E0.rect.top"),sQuery(id+"F0.wireOp",EDGE,"E0.rect.left"),sQuery(id+"F0.wireOp",EDGE,"E0.rect.right"),sQuery(id+"F0.wireOp",EDGE,"fb71736d-f74a-4242-934e-06f3cf912558.left"),subQ0,subQ1,sQuery(id+"F0.wireOp",EDGE,"E2.bottom"),sQuery(id+"F0.wireOp",EDGE,"E2.left"),sQuery(id+"F0.wireOp",EDGE,"E3.bottom"),sQuery(id+"F0.wireOp",EDGE,"E3.left"),sQuery(id+"F0.wireOp",EDGE,"E4"),sQuery(id+"F0.wireOp",EDGE,"E5"),sQuery(id+"F0.wireOp",EDGE,"E6"),sQuery(id+"F0.wireOp",EDGE,"E7"),sQuery(id+"F0.wireOp",EDGE,"E8"),sQuery(id+"F0.wireOp",EDGE,"E9.top"),sQuery(id+"F0.wireOp",EDGE,"E9.left"),sQuery(id+"F0.wireOp",EDGE,"E9.right"),sQuery(id+"F0.wireOp",EDGE,"E10.left"),sQuery(id+"F0.wireOp",EDGE,"E10.right"),sQuery(id+"F0.wireOp",EDGE,"E11.trimOffspring"),sQuery(id+"F0.wireOp",EDGE,"E10.top"),sQuery(id+"F0.wireOp",EDGE,"E27.top"),sQuery(id+"F0.wireOp",EDGE,"E27.left"),sQuery(id+"F0.wireOp",EDGE,"E27.right"),sQuery(id+"F0.wireOp",EDGE,"E14.top"),sQuery(id+"F0.wireOp",EDGE,"E12.right"),sQuery(id+"F0.wireOp",EDGE,"E14.right"),sQuery(id+"F0.wireOp",EDGE,"c10e0dd7-fc39-4358-877f-853744283f95"),sQuery(id+"F0.wireOp",EDGE,"E15.left"),sQuery(id+"F0.wireOp",EDGE,"E15.right"),sQuery(id+"F0.wireOp",EDGE,"b61ca566-ba07-4bff-9836-ffdb72489c4c.left"),sQuery(id+"F0.wireOp",EDGE,"b61ca566-ba07-4bff-9836-ffdb72489c4c.right"),sQuery(id+"F0.wireOp",EDGE,"E16.top"),sQuery(id+"F0.wireOp",EDGE,"E16.left"),sQuery(id+"F0.wireOp",EDGE,"E16.right"),sQuery(id+"F0.wireOp",EDGE,"E17.trimOffspring"),sQuery(id+"F0.wireOp",EDGE,"E18.trimOffspring"),sQuery(id+"F0.wireOp",EDGE,"54661143-fa5e-42c1-9d10-70f3552f3fbd"),sQuery(id+"F0.wireOp",EDGE,"E28"),sQuery(id+"F0.wireOp",EDGE,"E20"),sQuery(id+"F0.wireOp",EDGE,"E21")])],"isStart":false})]});}
            var Q8;
            Q8=makeQuery(id+"F1.opExtrude","CAP_EDGE",EDGE,{"disambiguationData":[OSD([sQuery(id+"F0.wireOp",EDGE,"E5")])],"isStart":false});
            var Q9;
            Q9=makeQuery(id+"F1.opExtrude","CAP_EDGE",EDGE,{"disambiguationData":[OSD([sQuery(id+"F0.wireOp",EDGE,"E6")])],"isStart":false});
            var Q10;
            Q10=makeQuery(id+"F1.opExtrude","CAP_EDGE",EDGE,{"disambiguationData":[OSD([sQuery(id+"F0.wireOp",EDGE,"E4")])],"isStart":false});
            var Q11;
            Q11=makeQuery(id+"F1.opExtrude","CAP_EDGE",EDGE,{"disambiguationData":[OSD([sQuery(id+"F0.wireOp",EDGE,"E7")])],"isStart":false});
            var Q12;
            Q12=makeQuery(id+"F1.opExtrude","CAP_EDGE",EDGE,{"disambiguationData":[OSD([sQuery(id+"F0.wireOp",EDGE,"E27.top")])],"isStart":false});
            var Q13;
            Q13=makeQuery(id+"F1.opExtrude","CAP_EDGE",EDGE,{"disambiguationData":[OSD([sQuery(id+"F0.wireOp",EDGE,"E27.right"),sQuery(id+"F0.wireOp",EDGE,"E15.left")])],"isStart":false});
            var Q14;
            Q14=makeQuery(id+"F1.opExtrude","CAP_EDGE",EDGE,{"disambiguationData":[OSD([sQuery(id+"F0.wireOp",EDGE,"E10.right"),sQuery(id+"F0.wireOp",EDGE,"E27.left")])],"isStart":false});
            var Q15;
            Q15=makeQuery(id+"F1.opExtrude","CAP_EDGE",EDGE,{"disambiguationData":[OSD([sQuery(id+"F0.wireOp",EDGE,"E11.trimOffspring")])],"isStart":false});
            var Q16;
            Q16=makeQuery(id+"F1.opExtrude","CAP_EDGE",EDGE,{"disambiguationData":[OSD([sQuery(id+"F0.wireOp",EDGE,"E9.right")])],"isStart":false});
            var Q17;
            Q17=makeQuery(id+"F1.opExtrude","CAP_EDGE",EDGE,{"disambiguationData":[OSD([sQuery(id+"F0.wireOp",EDGE,"E8"),sQuery(id+"F0.wireOp",EDGE,"E17.trimOffspring"),sQuery(id+"F0.wireOp",EDGE,"E18.trimOffspring"),sQuery(id+"F0.wireOp",EDGE,"E20"),sQuery(id+"F0.wireOp",EDGE,"E21")])],"isStart":false});
            var Q18;
            Q18=makeQuery(id+"F1.opExtrude","CAP_EDGE",EDGE,{"disambiguationData":[OSD([sQuery(id+"F0.wireOp",EDGE,"E9.left")])],"isStart":false});
            var Q19;
            Q19=makeQuery(id+"F1.opExtrude","CAP_EDGE",EDGE,{"disambiguationData":[OSD([sQuery(id+"F0.wireOp",EDGE,"E9.top")])],"isStart":false});
            var Q20;
            Q20=makeQuery(id+"F1.opExtrude","CAP_EDGE",EDGE,{"disambiguationData":[OSD([sQuery(id+"F0.wireOp",EDGE,"E10.left")])],"isStart":false});
            var Q21;
            Q21=makeQuery(id+"F1.opExtrude","CAP_EDGE",EDGE,{"disambiguationData":[OSD([sQuery(id+"F0.wireOp",EDGE,"E10.top")])],"isStart":false});
            var Q22;
            Q22=makeQuery(id+"F1.opExtrude","CAP_EDGE",EDGE,{"disambiguationData":[OSD([sQuery(id+"F0.wireOp",EDGE,"E12.right")])],"isStart":false});
            var Q23;
            Q23=makeQuery(id+"F1.opExtrude","CAP_EDGE",EDGE,{"disambiguationData":[OSD([sQuery(id+"F0.wireOp",EDGE,"E14.top")])],"isStart":false});
            var Q24;
            Q24=makeQuery(id+"F1.opExtrude","CAP_EDGE",EDGE,{"disambiguationData":[OSD([sQuery(id+"F0.wireOp",EDGE,"E14.right"),sQuery(id+"F0.wireOp",EDGE,"b61ca566-ba07-4bff-9836-ffdb72489c4c.left")])],"isStart":false});
            var Q25;
            Q25=makeQuery(id+"F1.opExtrude","CAP_EDGE",EDGE,{"disambiguationData":[OSD([sQuery(id+"F0.wireOp",EDGE,"54661143-fa5e-42c1-9d10-70f3552f3fbd")])],"isStart":false});
            var Q26;
            Q26=makeQuery(id+"F1.opExtrude","CAP_EDGE",EDGE,{"disambiguationData":[OSD([sQuery(id+"F0.wireOp",EDGE,"b61ca566-ba07-4bff-9836-ffdb72489c4c.right"),sQuery(id+"F0.wireOp",EDGE,"E16.left")])],"isStart":false});
            var Q27;
            Q27=makeQuery(id+"F1.opExtrude","CAP_EDGE",EDGE,{"disambiguationData":[OSD([sQuery(id+"F0.wireOp",EDGE,"E16.top")])],"isStart":false});
            var Q28;
            Q28=makeQuery(id+"F1.opExtrude","CAP_EDGE",EDGE,{"disambiguationData":[OSD([sQuery(id+"F0.wireOp",EDGE,"E15.right"),sQuery(id+"F0.wireOp",EDGE,"E16.right")])],"isStart":false});
            var Q29;
            Q29=makeQuery(id+"F1.opExtrude","CAP_EDGE",EDGE,{"disambiguationData":[OSD([sQuery(id+"F0.wireOp",EDGE,"E28")])],"isStart":false});
            var Q30;
            Q30=makeQuery(id+"F1.opExtrude","CAP_EDGE",EDGE,{"disambiguationData":[OSD([sQuery(id+"F0.wireOp",EDGE,"E23.top"),sQuery(id+"F0.wireOp",EDGE,"E32")])],"isStart":false});
            var Q31;
            Q31=makeQuery(id+"F1.opExtrude","CAP_EDGE",EDGE,{"disambiguationData":[OSD([sQuery(id+"F0.wireOp",EDGE,"E22.right")])],"isStart":false});
            var Q32;
            Q32=makeQuery(id+"F1.opExtrude","CAP_EDGE",EDGE,{"disambiguationData":[OSD([sQuery(id+"F0.wireOp",EDGE,"E30")])],"isStart":false});
            var Q33;
            {var subQ0=sQuery(id+"F0.wireOp",EDGE,"E22.right");var subQ1=sQuery(id+"F0.wireOp",EDGE,"E32");var subQ2=sQuery(id+"F0.wireOp",EDGE,"E23.top");var subQ3=sQuery(id+"F0.wireOp",EDGE,"E30");var subQ4=sQuery(id+"F0.wireOp",EDGE,"E7");var subQ5=sQuery(id+"F0.wireOp",EDGE,"E2.left");var subQ6=sQuery(id+"F0.wireOp",EDGE,"E2.bottom");var subQ7=sQuery(id+"F0.wireOp",EDGE,"E9.top");var subQ8=sQuery(id+"F0.wireOp",EDGE,"c10e0dd7-fc39-4358-877f-853744283f95");var subQ9=sQuery(id+"F0.wireOp",EDGE,"fb71736d-f74a-4242-934e-06f3cf912558.left");var subQ10=sQuery(id+"F0.wireOp",EDGE,"E1.left");var subQ11=sQuery(id+"F0.wireOp",EDGE,"E1.bottom");var subQ12=sQuery(id+"F0.wireOp",EDGE,"E10.top");var subQ13=sQuery(id+"F0.wireOp",EDGE,"E6");var subQ14=sQuery(id+"F0.wireOp",EDGE,"E5");var subQ15=sQuery(id+"F0.wireOp",EDGE,"E4");var subQ16=sQuery(id+"F0.wireOp",EDGE,"E16.top");var subQ17=sQuery(id+"F0.wireOp",EDGE,"E3.bottom");var subQ18=sQuery(id+"F0.wireOp",EDGE,"E0.rect.bottom");var subQ19=sQuery(id+"F0.wireOp",EDGE,"E0.rect.top");var subQ20=sQuery(id+"F0.wireOp",EDGE,"E9.right");var subQ21=sQuery(id+"F0.wireOp",EDGE,"E3.left");var subQ22=sQuery(id+"F0.wireOp",EDGE,"E12.right");var subQ23=sQuery(id+"F0.wireOp",EDGE,"E21");var subQ24=sQuery(id+"F0.wireOp",EDGE,"E20");var subQ25=sQuery(id+"F0.wireOp",EDGE,"E18.trimOffspring");var subQ26=sQuery(id+"F0.wireOp",EDGE,"E17.trimOffspring");var subQ27=sQuery(id+"F0.wireOp",EDGE,"E8");var subQ28=sQuery(id+"F0.wireOp",EDGE,"E16.right");var subQ29=sQuery(id+"F0.wireOp",EDGE,"E15.right");var subQ30=sQuery(id+"F0.wireOp",EDGE,"E29.top");var subQ31=sQuery(id+"F0.wireOp",EDGE,"E14.top");var subQ32=sQuery(id+"F0.wireOp",EDGE,"E0.rect.left");var subQ33=sQuery(id+"F0.wireOp",EDGE,"E0.rect.right");var subQ34=sQuery(id+"F0.wireOp",EDGE,"E9.left");var subQ35=sQuery(id+"F0.wireOp",EDGE,"E22.bottom");var subQ36=sQuery(id+"F0.wireOp",EDGE,"E11.trimOffspring");var subQ37=sQuery(id+"F0.wireOp",EDGE,"E10.left");Q33=makeQuery(id+"F4.boolean.opBoolean","SPLIT",FACE,{"disambiguationData":[TD([makeQuery(id+"F1.opExtrude","SWEPT_FACE",FACE,{"disambiguationData":[OSD([subQ15])]})])],"derivedFrom":makeQuery(id+"F1.opExtrude","CAP_FACE",FACE,{"disambiguationData":[OSD([subQ18,subQ19,subQ32,subQ33,subQ9,subQ11,subQ10,subQ6,subQ5,subQ17,subQ21,subQ15,subQ14,subQ13,subQ4,subQ27,subQ7,subQ34,subQ20,subQ37,subQ36,subQ12,subQ31,subQ22,subQ8,subQ29,subQ16,subQ28,subQ26,subQ25,subQ24,subQ23,subQ35,subQ2,subQ0,subQ1,subQ30,subQ3])],"isStart":false})});}
            var Q34;
            Q34=makeQuery(id+"F1.opExtrude","SWEPT_EDGE",EDGE,{"disambiguationData":[OSD([sQuery(id+"F0.wireOp",EDGE,"E10.top"),sQuery(id+"F0.wireOp",EDGE,"E12.right")])]});
            var Q35;
            Q35=makeQuery(id+"F1.opExtrude","SWEPT_EDGE",EDGE,{"disambiguationData":[OSD([sQuery(id+"F0.wireOp",EDGE,"E29.top"),sQuery(id+"F0.wireOp",EDGE,"E30")])]});
            var Q36;
            Q36=makeQuery(id+"F1.opExtrude","SWEPT_EDGE",EDGE,{"disambiguationData":[OSD([sQuery(id+"F0.wireOp",EDGE,"E9.top"),sQuery(id+"F0.wireOp",EDGE,"E10.left")])]});
            var Q37;
            Q37=makeQuery(id+"F1.opExtrude","SWEPT_EDGE",EDGE,{"disambiguationData":[OSD([sQuery(id+"F0.wireOp",EDGE,"E15.right"),sQuery(id+"F0.wireOp",EDGE,"E32")])]});
            var Q38;
            Q38=makeQuery(id+"F1.opExtrude","SWEPT_EDGE",EDGE,{"disambiguationData":[OSD([sQuery(id+"F0.wireOp",EDGE,"E22.bottom"),sQuery(id+"F0.wireOp",EDGE,"E22.right")])]});
            var Q39;
            Q39=makeQuery(id+"F1.opExtrude","CAP_EDGE",EDGE,{"disambiguationData":[OSD([sQuery(id+"F0.wireOp",EDGE,"E9.top")])],"isStart":true});
            var Q40;
            Q40=makeQuery(id+"F1.opExtrude","CAP_EDGE",EDGE,{"disambiguationData":[OSD([sQuery(id+"F0.wireOp",EDGE,"E9.left")])],"isStart":true});
            var Q41;
            Q41=makeQuery(id+"F1.opExtrude","CAP_EDGE",EDGE,{"disambiguationData":[OSD([sQuery(id+"F0.wireOp",EDGE,"E10.left")])],"isStart":true});
            var Q42;
            Q42=makeQuery(id+"F1.opExtrude","CAP_EDGE",EDGE,{"disambiguationData":[OSD([sQuery(id+"F0.wireOp",EDGE,"E10.top")])],"isStart":true});
            var Q43;
            Q43=makeQuery(id+"F1.opExtrude","CAP_EDGE",EDGE,{"disambiguationData":[OSD([sQuery(id+"F0.wireOp",EDGE,"E12.right")])],"isStart":true});
            var Q44;
            Q44=makeQuery(id+"F1.opExtrude","CAP_EDGE",EDGE,{"disambiguationData":[OSD([sQuery(id+"F0.wireOp",EDGE,"E14.top"),sQuery(id+"F0.wireOp",EDGE,"E29.top")])],"isStart":true});
            var Q45;
            Q45=makeQuery(id+"F1.opExtrude","CAP_EDGE",EDGE,{"disambiguationData":[OSD([sQuery(id+"F0.wireOp",EDGE,"E30")])],"isStart":true});
            var Q46;
            Q46=makeQuery(id+"F1.opExtrude","CAP_EDGE",EDGE,{"disambiguationData":[OSD([sQuery(id+"F0.wireOp",EDGE,"E16.top")])],"isStart":true});
            var Q47;
            Q47=makeQuery(id+"F1.opExtrude","CAP_EDGE",EDGE,{"disambiguationData":[OSD([sQuery(id+"F0.wireOp",EDGE,"E8"),sQuery(id+"F0.wireOp",EDGE,"E17.trimOffspring"),sQuery(id+"F0.wireOp",EDGE,"E18.trimOffspring"),sQuery(id+"F0.wireOp",EDGE,"E20"),sQuery(id+"F0.wireOp",EDGE,"E21")])],"isStart":true});
            var Q48;
            Q48=makeQuery(id+"F1.opExtrude","CAP_EDGE",EDGE,{"disambiguationData":[OSD([sQuery(id+"F0.wireOp",EDGE,"E15.right"),sQuery(id+"F0.wireOp",EDGE,"E16.right")])],"isStart":true});
            var Q49;
            Q49=makeQuery(id+"F1.opExtrude","CAP_EDGE",EDGE,{"disambiguationData":[OSD([sQuery(id+"F0.wireOp",EDGE,"E23.top"),sQuery(id+"F0.wireOp",EDGE,"E32")])],"isStart":true});
            var Q50;
            Q50=makeQuery(id+"F1.opExtrude","CAP_EDGE",EDGE,{"disambiguationData":[OSD([sQuery(id+"F0.wireOp",EDGE,"E22.right")])],"isStart":true});
            var Q51;
            Q51=makeQuery(id+"F1.opExtrude","CAP_EDGE",EDGE,{"disambiguationData":[OSD([sQuery(id+"F0.wireOp",EDGE,"E11.trimOffspring"),sQuery(id+"F0.wireOp",EDGE,"E22.bottom")])],"isStart":true});
            var Q52;
            Q52=makeQuery(id+"F1.opExtrude","CAP_EDGE",EDGE,{"disambiguationData":[OSD([sQuery(id+"F0.wireOp",EDGE,"E9.right")])],"isStart":true});
            var Q53;
            Q53=makeQuery(id+"F1.opExtrude","CAP_EDGE",EDGE,{"disambiguationData":[OSD([sQuery(id+"F0.wireOp",EDGE,"E31.top")])],"isStart":true});
            var Q54;
            Q54=makeQuery(id+"F1.opExtrude","SWEPT_EDGE",EDGE,{"disambiguationData":[OSD([sQuery(id+"F0.wireOp",EDGE,"E16.right"),sQuery(id+"F0.wireOp",EDGE,"E31.top")])]});
            chamfer(context, id + "F6", {"entities" : qUnion([Q0, Q1, Q2, Q3, Q4, Q5, Q6, Q7, Q8, Q9, Q10, Q11, Q12, Q13, Q14, Q15, Q16, Q17, Q18, Q19, Q20, Q21, Q22, Q23, Q24, Q25, Q26, Q27, Q28, Q29, Q30, Q31, Q32, Q33, Q34, Q35, Q36, Q37, Q38, Q39, Q40, Q41, Q42, Q43, Q44, Q45, Q46, Q47, Q48, Q49, Q50, Q51, Q52, Q53, Q54]), "width" : .4 * mm, "tangentPropagation" : true});
        }
        {
            var Q0;
            Q0=makeQuery(id+"F1.opExtrude","CAP_FACE",FACE,{"disambiguationData":[OSD([sQuery(id+"F0.wireOp",EDGE,"E0.rect.bottom"),sQuery(id+"F0.wireOp",EDGE,"E0.rect.top"),sQuery(id+"F0.wireOp",EDGE,"E0.rect.left"),sQuery(id+"F0.wireOp",EDGE,"E0.rect.right"),sQuery(id+"F0.wireOp",EDGE,"fb71736d-f74a-4242-934e-06f3cf912558.left"),sQuery(id+"F0.wireOp",EDGE,"E1.bottom"),sQuery(id+"F0.wireOp",EDGE,"E1.left"),sQuery(id+"F0.wireOp",EDGE,"E2.bottom"),sQuery(id+"F0.wireOp",EDGE,"E2.left"),sQuery(id+"F0.wireOp",EDGE,"E3.bottom"),sQuery(id+"F0.wireOp",EDGE,"E3.left"),sQuery(id+"F0.wireOp",EDGE,"E4"),sQuery(id+"F0.wireOp",EDGE,"E5"),sQuery(id+"F0.wireOp",EDGE,"E6"),sQuery(id+"F0.wireOp",EDGE,"E7"),sQuery(id+"F0.wireOp",EDGE,"E8"),sQuery(id+"F0.wireOp",EDGE,"E9.top"),sQuery(id+"F0.wireOp",EDGE,"E9.left"),sQuery(id+"F0.wireOp",EDGE,"E9.right"),sQuery(id+"F0.wireOp",EDGE,"E10.left"),sQuery(id+"F0.wireOp",EDGE,"E10.right"),sQuery(id+"F0.wireOp",EDGE,"E11.trimOffspring"),sQuery(id+"F0.wireOp",EDGE,"E10.top"),sQuery(id+"F0.wireOp",EDGE,"E27.top"),sQuery(id+"F0.wireOp",EDGE,"E27.left"),sQuery(id+"F0.wireOp",EDGE,"E27.right"),sQuery(id+"F0.wireOp",EDGE,"E14.top"),sQuery(id+"F0.wireOp",EDGE,"E12.right"),sQuery(id+"F0.wireOp",EDGE,"E14.right"),sQuery(id+"F0.wireOp",EDGE,"c10e0dd7-fc39-4358-877f-853744283f95"),sQuery(id+"F0.wireOp",EDGE,"E15.left"),sQuery(id+"F0.wireOp",EDGE,"E15.right"),sQuery(id+"F0.wireOp",EDGE,"b61ca566-ba07-4bff-9836-ffdb72489c4c.left"),sQuery(id+"F0.wireOp",EDGE,"b61ca566-ba07-4bff-9836-ffdb72489c4c.right"),sQuery(id+"F0.wireOp",EDGE,"E16.top"),sQuery(id+"F0.wireOp",EDGE,"E16.left"),sQuery(id+"F0.wireOp",EDGE,"E16.right"),sQuery(id+"F0.wireOp",EDGE,"E17.trimOffspring"),sQuery(id+"F0.wireOp",EDGE,"E18.trimOffspring"),sQuery(id+"F0.wireOp",EDGE,"54661143-fa5e-42c1-9d10-70f3552f3fbd"),sQuery(id+"F0.wireOp",EDGE,"E28"),sQuery(id+"F0.wireOp",EDGE,"E20"),sQuery(id+"F0.wireOp",EDGE,"E21")])],"isStart":true});
            var Q1;
            {var subQ0=sQuery(id+"F0.wireOp",EDGE,"E33");var subQ1=sQuery(id+"F0.wireOp",EDGE,"E1.bottom");Q1=makeQuery(id+"F2.opFillet","BLEND_EDGE",EDGE,{"blendedFrom":[makeQuery(id+"F1.opExtrude","SWEPT_EDGE",EDGE,{"disambiguationData":[OSD([subQ1,subQ0])]}),makeQuery(id+"F1.opExtrude","CAP_FACE",FACE,{"disambiguationData":[OSD([sQuery(id+"F0.wireOp",EDGE,"E0.rect.top"),sQuery(id+"F0.wireOp",EDGE,"E0.rect.right"),subQ1,sQuery(id+"F0.wireOp",EDGE,"E2.bottom"),sQuery(id+"F0.wireOp",EDGE,"E2.left"),sQuery(id+"F0.wireOp",EDGE,"E3.left"),sQuery(id+"F0.wireOp",EDGE,"E4"),sQuery(id+"F0.wireOp",EDGE,"E5"),sQuery(id+"F0.wireOp",EDGE,"E6"),sQuery(id+"F0.wireOp",EDGE,"E7"),sQuery(id+"F0.wireOp",EDGE,"E8"),sQuery(id+"F0.wireOp",EDGE,"E9.top"),sQuery(id+"F0.wireOp",EDGE,"E9.left"),sQuery(id+"F0.wireOp",EDGE,"E9.right"),sQuery(id+"F0.wireOp",EDGE,"E10.left"),sQuery(id+"F0.wireOp",EDGE,"E11.trimOffspring"),sQuery(id+"F0.wireOp",EDGE,"E10.top"),sQuery(id+"F0.wireOp",EDGE,"E14.top"),sQuery(id+"F0.wireOp",EDGE,"E12.right"),sQuery(id+"F0.wireOp",EDGE,"E16.top"),sQuery(id+"F0.wireOp",EDGE,"E16.right"),sQuery(id+"F0.wireOp",EDGE,"E17.trimOffspring"),sQuery(id+"F0.wireOp",EDGE,"E18.trimOffspring"),sQuery(id+"F0.wireOp",EDGE,"E20"),sQuery(id+"F0.wireOp",EDGE,"E21"),sQuery(id+"F0.wireOp",EDGE,"E22.bottom"),sQuery(id+"F0.wireOp",EDGE,"E22.right"),sQuery(id+"F0.wireOp",EDGE,"E29.top"),sQuery(id+"F0.wireOp",EDGE,"E30"),sQuery(id+"F0.wireOp",EDGE,"E31.top"),sQuery(id+"F0.wireOp",EDGE,"E31.right"),subQ0,sQuery(id+"F0.wireOp",EDGE,"E35")])],"isStart":true})],"blendedInto":[makeQuery(id+"F1.opExtrude","CAP_FACE",FACE,{"disambiguationData":[OSD([sQuery(id+"F0.wireOp",EDGE,"E0.rect.top"),sQuery(id+"F0.wireOp",EDGE,"E0.rect.right"),subQ1,sQuery(id+"F0.wireOp",EDGE,"E2.bottom"),sQuery(id+"F0.wireOp",EDGE,"E2.left"),sQuery(id+"F0.wireOp",EDGE,"E3.left"),sQuery(id+"F0.wireOp",EDGE,"E4"),sQuery(id+"F0.wireOp",EDGE,"E5"),sQuery(id+"F0.wireOp",EDGE,"E6"),sQuery(id+"F0.wireOp",EDGE,"E7"),sQuery(id+"F0.wireOp",EDGE,"E8"),sQuery(id+"F0.wireOp",EDGE,"E9.top"),sQuery(id+"F0.wireOp",EDGE,"E9.left"),sQuery(id+"F0.wireOp",EDGE,"E9.right"),sQuery(id+"F0.wireOp",EDGE,"E10.left"),sQuery(id+"F0.wireOp",EDGE,"E11.trimOffspring"),sQuery(id+"F0.wireOp",EDGE,"E10.top"),sQuery(id+"F0.wireOp",EDGE,"E14.top"),sQuery(id+"F0.wireOp",EDGE,"E12.right"),sQuery(id+"F0.wireOp",EDGE,"E16.top"),sQuery(id+"F0.wireOp",EDGE,"E16.right"),sQuery(id+"F0.wireOp",EDGE,"E17.trimOffspring"),sQuery(id+"F0.wireOp",EDGE,"E18.trimOffspring"),sQuery(id+"F0.wireOp",EDGE,"E20"),sQuery(id+"F0.wireOp",EDGE,"E21"),sQuery(id+"F0.wireOp",EDGE,"E22.bottom"),sQuery(id+"F0.wireOp",EDGE,"E22.right"),sQuery(id+"F0.wireOp",EDGE,"E29.top"),sQuery(id+"F0.wireOp",EDGE,"E30"),sQuery(id+"F0.wireOp",EDGE,"E31.top"),sQuery(id+"F0.wireOp",EDGE,"E31.right"),subQ0,sQuery(id+"F0.wireOp",EDGE,"E35")])],"isStart":true})]});}
            chamfer(context, id + "F7", {"entities" : qUnion([Q0, Q1]), "width" : .4 * mm, "tangentPropagation" : true});
        }
        {
            var Q0;
            Q0=makeQuery(id+"F1.opExtrude","SWEPT_BODY",BODY,{"disambiguationData":[OSD([sQuery(id+"F0.wireOp",EDGE,"E0.rect.bottom"),sQuery(id+"F0.wireOp",EDGE,"E0.rect.top"),sQuery(id+"F0.wireOp",EDGE,"E0.rect.left"),sQuery(id+"F0.wireOp",EDGE,"E0.rect.right"),sQuery(id+"F0.wireOp",EDGE,"fb71736d-f74a-4242-934e-06f3cf912558.left"),sQuery(id+"F0.wireOp",EDGE,"E1.bottom"),sQuery(id+"F0.wireOp",EDGE,"E1.left"),sQuery(id+"F0.wireOp",EDGE,"E2.bottom"),sQuery(id+"F0.wireOp",EDGE,"E2.left"),sQuery(id+"F0.wireOp",EDGE,"E3.bottom"),sQuery(id+"F0.wireOp",EDGE,"E3.left"),sQuery(id+"F0.wireOp",EDGE,"E4"),sQuery(id+"F0.wireOp",EDGE,"E5"),sQuery(id+"F0.wireOp",EDGE,"E6"),sQuery(id+"F0.wireOp",EDGE,"E7"),sQuery(id+"F0.wireOp",EDGE,"E8"),sQuery(id+"F0.wireOp",EDGE,"E9.top"),sQuery(id+"F0.wireOp",EDGE,"E9.left"),sQuery(id+"F0.wireOp",EDGE,"E9.right"),sQuery(id+"F0.wireOp",EDGE,"E10.left"),sQuery(id+"F0.wireOp",EDGE,"E10.right"),sQuery(id+"F0.wireOp",EDGE,"E11.trimOffspring"),sQuery(id+"F0.wireOp",EDGE,"E10.top"),sQuery(id+"F0.wireOp",EDGE,"E27.top"),sQuery(id+"F0.wireOp",EDGE,"E27.left"),sQuery(id+"F0.wireOp",EDGE,"E27.right"),sQuery(id+"F0.wireOp",EDGE,"E14.top"),sQuery(id+"F0.wireOp",EDGE,"E12.right"),sQuery(id+"F0.wireOp",EDGE,"E14.right"),sQuery(id+"F0.wireOp",EDGE,"c10e0dd7-fc39-4358-877f-853744283f95"),sQuery(id+"F0.wireOp",EDGE,"E15.left"),sQuery(id+"F0.wireOp",EDGE,"E15.right"),sQuery(id+"F0.wireOp",EDGE,"b61ca566-ba07-4bff-9836-ffdb72489c4c.left"),sQuery(id+"F0.wireOp",EDGE,"b61ca566-ba07-4bff-9836-ffdb72489c4c.right"),sQuery(id+"F0.wireOp",EDGE,"E16.top"),sQuery(id+"F0.wireOp",EDGE,"E16.left"),sQuery(id+"F0.wireOp",EDGE,"E16.right"),sQuery(id+"F0.wireOp",EDGE,"E17.trimOffspring"),sQuery(id+"F0.wireOp",EDGE,"E18.trimOffspring"),sQuery(id+"F0.wireOp",EDGE,"54661143-fa5e-42c1-9d10-70f3552f3fbd"),sQuery(id+"F0.wireOp",EDGE,"E28"),sQuery(id+"F0.wireOp",EDGE,"E20"),sQuery(id+"F0.wireOp",EDGE,"E21")])]});
            var Q1;
            {var subQ0=sQuery(id+"F0.wireOp",EDGE,"E0.rect.top");var subQ1=sQuery(id+"F0.wireOp",EDGE,"E1.bottom");var subQ2=sQuery(id+"F0.wireOp",EDGE,"E2.bottom");Q1=makeQuery(id+"F7.opChamfer","BLEND_EDGE",EDGE,{"blendedFrom":[makeQuery(id+"F1.opExtrude","CAP_EDGE",EDGE,{"disambiguationData":[OSD([subQ0,subQ1,subQ2])],"isStart":true}),makeQuery(id+"F1.opExtrude","SWEPT_FACE",FACE,{"disambiguationData":[OSD([subQ0,subQ1,subQ2])]})],"blendedInto":[makeQuery(id+"F1.opExtrude","SWEPT_FACE",FACE,{"disambiguationData":[OSD([subQ0,subQ1,subQ2])]})]});}
            transform(context, id + "F8", {"entities" : qUnion([Q0]), "transformType" : TransformType.ROTATION, "transformAxis" : qUnion([Q1]), "angle" : 180 * degree, "makeCopy" : false});
        }
    });
